# Revit family: Desks-Teknion-B_RDF_Rectangular_Peninsula_Desk_with_Half_Modesty-R2019
name_source: partatom
category: Furniture
units: mm (PartAtom-declared; Revit-internal decimal feet)

## family parameters
Always vertical = Yes
Cut with Voids When Loaded = No
OmniClass Number = 23.40.20.00
OmniClass Title = General Furniture and Specialties
Room Calculation Point = No
Shared = Yes
Work Plane-Based = No

## types (3) — shared parameters
Assembly Code = E2020200
Manufacturer = Teknion
Manufacturer Fax = 416.661.4586
Part Number = B_RDF
Product Documentation Link = https://www.teknion.com
Product Line = Expansion Casegoods
Product Page URL = https://www.teknion.com
Series = Expansion Casegoods
Sustainability Data = https://www.teknion.com
URL = www.teknion.com
Unit Weight URL = http://www.teknion.com
Warranty = http://www.teknion.com

## per-type parameters (varying)
| type | Description | Height | Model | Worksurface Thickness |
| 1 3/16" Worksurface Thickness | Rectangular Peninsula Desk with Half Modesty, 1 3/16" Worksurface Thickness | 28.996 " | BMRDF_____ | 1.189 " |
| 1" Worksurface Thickness | Rectangular Peninsula Desk with Half Modesty, 1" Worksurface Thickness | 28.823 " | BDRDF_____ | 1.016 " |
| 1 9/16" Worksurface Thickness | Rectangular Peninsula Desk with Half Modesty, 1 9/16" Worksurface Thickness | 29.362 " | BXRDF_____ | 1.555 " |

## geometry (parser evidence)
native form markers: Sweep x2
no freeform markers — native parametric forms only
